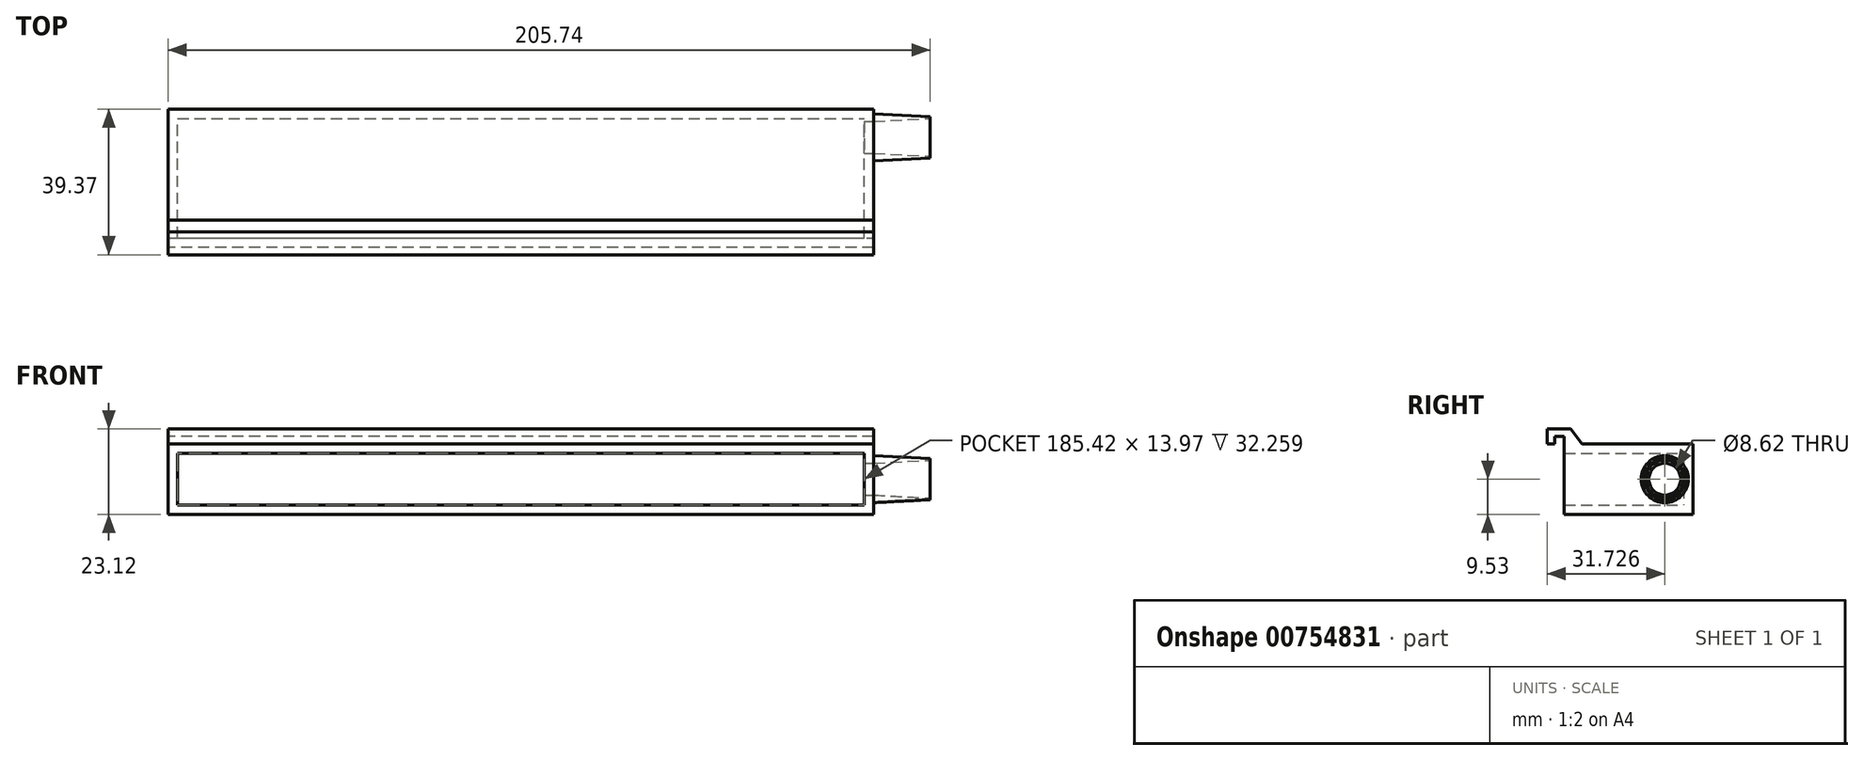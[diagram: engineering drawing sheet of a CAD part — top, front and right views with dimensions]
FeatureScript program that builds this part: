
annotation { "Feature Type Name" : "Feature", "Feature Type Description" : "" }
export const myFeature = defineFeature(function(context is Context, id is Id, definition is map)
    precondition{}
    {
        {
            var Q0;
            Q0=qCreatedBy(makeId("Front.planeOp"),FACE);
            var sketch = newSketch(context, id + "F0", { "sketchPlane" : qUnion([Q0])});
            skLineSegment(sketch, "E0.bottom", {"start": v(-95.25, 9.52) * mm, "end": v(95.25, 9.52) * mm});
            skLineSegment(sketch, "E0.top", {"start": v(-95.25, -9.52) * mm, "end": v(95.25, -9.52) * mm});
            skLineSegment(sketch, "E0.left", {"start": v(-95.25, 9.52) * mm, "end": v(-95.25, -9.52) * mm});
            skLineSegment(sketch, "E0.right", {"start": v(95.25, 9.52) * mm, "end": v(95.25, -9.52) * mm});
            skPoint(sketch, "E0.middle", {"position": v(0, 0) * mm});
            skLineSegment(sketch, "E1.bottom", {"start": v(-92.7, 6.98) * mm, "end": v(92.71, 6.99) * mm});
            skLineSegment(sketch, "E1.top", {"start": v(-92.71, -6.99) * mm, "end": v(92.7, -6.98) * mm});
            skLineSegment(sketch, "E1.left", {"start": v(-92.7, 6.98) * mm, "end": v(-92.7, -6.99) * mm});
            skLineSegment(sketch, "E1.right", {"start": v(92.71, 6.99) * mm, "end": v(92.71, -6.98) * mm});
            skSolve(sketch);
        }
        {
            var Q0;
            Q0=makeQuery(id+"F0.imprint","IMPRINT",FACE,{"disambiguationData":[TD([[makeQuery(id+"F0.imprint","IMPRINT",EDGE,{"derivedFrom":sQuery(id+"F0.wireOp",EDGE,"E0.bottom")}),-1.0]])]});
            extrude(context, id + "F1", {"entities" : qUnion([Q0]), "depth" : 63.5 * mm, "offsetDistance" : 25.4 * mm});
        }
        {
            var Q0;
            Q0=makeQuery(id+"F0.imprint","IMPRINT",FACE,{"disambiguationData":[TD([[makeQuery(id+"F0.imprint","IMPRINT",EDGE,{"derivedFrom":sQuery(id+"F0.wireOp",EDGE,"E1.bottom")}),-1.0]])]});
            extrude(context, id + "F2", {"entities" : qUnion([Q0]), "operationType" : NewBodyOperationType.ADD, "depth" : 2.54 * mm, "offsetDistance" : 25.4 * mm});
        }
        {
            var Q0;
            Q0=makeQuery(id+"F1.opExtrude","SWEPT_FACE",FACE,{"disambiguationData":[OSD([sQuery(id+"F0.wireOp",EDGE,"E0.right")])]});
            var sketch = newSketch(context, id + "F3", { "sketchPlane" : qUnion([Q0])});
            skCircle(sketch, "E2", {"center": v(-7.64, 0) * mm, "radius": 6.35 * mm});
            skCircle(sketch, "E3", {"center": v(-7.64, 0) * mm, "radius": 4.31 * mm});
            skSolve(sketch);
        }
        {
            var Q0;
            Q0=makeQuery(id+"F3.imprint","IMPRINT",FACE,{"disambiguationData":[TD([[makeQuery(id+"F3.imprint","IMPRINT",EDGE,{"derivedFrom":sQuery(id+"F3.wireOp",EDGE,"E3")}),1.0]])]});
            extrude(context, id + "F4", {"entities" : qUnion([Q0]), "operationType" : NewBodyOperationType.REMOVE, "oppositeDirection" : true, "depth" : 25.4 * mm, "offsetDistance" : 25.4 * mm});
        }
        {
            var Q0;
            Q0=makeQuery(id+"F3.imprint","IMPRINT",FACE,{"disambiguationData":[TD([[makeQuery(id+"F3.imprint","IMPRINT",EDGE,{"derivedFrom":sQuery(id+"F3.wireOp",EDGE,"E2")}),1.0]])]});
            extrude(context, id + "F5", {"entities" : qUnion([Q0]), "operationType" : NewBodyOperationType.ADD, "depth" : 15.24 * mm, "offsetDistance" : 25.4 * mm, "hasDraft" : true, "draftAngle" : 3 * degree, "draftPullDirection" : true});
        }
        {
            var Q0;
            Q0=makeQuery(id+"F1.opExtrude","SWEPT_FACE",FACE,{"disambiguationData":[OSD([sQuery(id+"F0.wireOp",EDGE,"E0.bottom")])]});
            var sketch = newSketch(context, id + "F6", { "sketchPlane" : qUnion([Q0])});
            skLineSegment(sketch, "E4", {"start": v(-95.25, -63.5) * mm, "end": v(-95.25, -68.3) * mm});
            skLineSegment(sketch, "E5", {"start": v(-95.25, -68.3) * mm, "end": v(-89.5, -68.3) * mm});
            skLineSegment(sketch, "E6", {"start": v(-89.5, -68.3) * mm, "end": v(-89.5, -66.04) * mm});
            skLineSegment(sketch, "E7", {"start": v(-89.5, -66.04) * mm, "end": v(-92.73, -66.04) * mm});
            skLineSegment(sketch, "E8", {"start": v(-92.73, -66.04) * mm, "end": v(-92.73, -63.5) * mm});
            skLineSegment(sketch, "E9", {"start": v(-92.73, -63.5) * mm, "end": v(-95.25, -63.5) * mm});
            skSolve(sketch);
        }
        {
            var Q0;
            Q0=makeQuery(id+"F6.imprint","IMPRINT",FACE,{"disambiguationData":[TD([[makeQuery(id+"F6.imprint","IMPRINT",EDGE,{"derivedFrom":sQuery(id+"F6.wireOp",EDGE,"E4")}),1.0]])]});
            extrude(context, id + "F7", {"entities" : qUnion([Q0]), "operationType" : NewBodyOperationType.ADD, "oppositeDirection" : true, "depth" : 19.05 * mm, "offsetDistance" : 25.4 * mm});
        }
        {
            var Q0;
            Q0=makeQuery(id+"F1.opExtrude","CAP_FACE",FACE,{"disambiguationData":[OSD([sQuery(id+"F0.wireOp",EDGE,"E0.bottom"),sQuery(id+"F0.wireOp",EDGE,"E0.top"),sQuery(id+"F0.wireOp",EDGE,"E0.left"),sQuery(id+"F0.wireOp",EDGE,"E0.right"),sQuery(id+"F0.wireOp",EDGE,"E1.bottom"),sQuery(id+"F0.wireOp",EDGE,"E1.top"),sQuery(id+"F0.wireOp",EDGE,"E1.left"),sQuery(id+"F0.wireOp",EDGE,"E1.right")])],"isStart":false});
            var sketch = newSketch(context, id + "F8", { "sketchPlane" : qUnion([Q0])});
            skLineSegment(sketch, "E10.bottom", {"start": v(-92.73, 9.52) * mm, "end": v(92.73, 9.52) * mm});
            skLineSegment(sketch, "E10.top", {"start": v(-92.73, 7.05) * mm, "end": v(92.73, 7.05) * mm});
            skLineSegment(sketch, "E10.left", {"start": v(-92.73, 9.52) * mm, "end": v(-92.73, 7.05) * mm});
            skLineSegment(sketch, "E10.right", {"start": v(92.73, 9.52) * mm, "end": v(92.73, 7.05) * mm});
            skPoint(sketch, "E10.middle", {"position": v(0, 8.29) * mm});
            skPoint(sketch, "E10.middle.positionSnap0", {"position": v(0, 6.99) * mm});
            skPoint(sketch, "E10.centerSnap0", {"position": v(0, 6.99) * mm});
            skSolve(sketch);
        }
        {
            var Q0;
            Q0=makeQuery(id+"F8.imprint","IMPRINT",FACE,{"disambiguationData":[TD([[makeQuery(id+"F8.imprint","IMPRINT",EDGE,{"derivedFrom":sQuery(id+"F8.wireOp",EDGE,"E10.bottom")}),-1.0]])]});
            extrude(context, id + "F9", {"entities" : qUnion([Q0]), "operationType" : NewBodyOperationType.ADD, "depth" : 12.7 * mm, "offsetDistance" : 25.4 * mm, "hasDraft" : true, "draftAngle" : 3 * degree, "draftPullDirection" : true});
        }
        {
            var Q0;
            Q0=qCreatedBy(makeId("Right.planeOp"),FACE);
            var sketch = newSketch(context, id + "F10", { "sketchPlane" : qUnion([Q0])});
            skLineSegment(sketch, "E11.bottom", {"start": v(-116.12, 21.47) * mm, "end": v(-34.8, 21.47) * mm});
            skLineSegment(sketch, "E11.top", {"start": v(-116.12, -21.47) * mm, "end": v(-34.8, -21.47) * mm});
            skLineSegment(sketch, "E11.left", {"start": v(-116.12, 21.47) * mm, "end": v(-116.12, -21.47) * mm});
            skLineSegment(sketch, "E11.right", {"start": v(-34.8, 21.47) * mm, "end": v(-34.8, -21.47) * mm});
            skPoint(sketch, "E11.middle", {"position": v(-75.46, 0) * mm});
            skSolve(sketch);
        }
        {
            var Q0;
            Q0=makeQuery(id+"F10.imprint","IMPRINT",FACE,{"disambiguationData":[TD([[makeQuery(id+"F10.imprint","IMPRINT",EDGE,{"derivedFrom":sQuery(id+"F10.wireOp",EDGE,"E11.bottom")}),-1.0]])]});
            extrude(context, id + "F11", {"entities" : qUnion([Q0]), "operationType" : NewBodyOperationType.REMOVE, "endBound" : BoundingType.SYMMETRIC, "oppositeDirection" : true, "depth" : 203.2 * mm, "offsetDistance" : 25.4 * mm});
        }
        {
            var Q0;
            Q0=makeQuery(id+"F7.boolean.opBoolean","MERGE",FACE,{"derivedFrom":[makeQuery(id+"F1.opExtrude","SWEPT_FACE",FACE,{"disambiguationData":[OSD([sQuery(id+"F0.wireOp",EDGE,"E0.left")])]}),makeQuery(id+"F7.opExtrude","SWEPT_FACE",FACE,{"disambiguationData":[OSD([sQuery(id+"F6.wireOp",EDGE,"E4")])]})]});
            var sketch = newSketch(context, id + "F12", { "sketchPlane" : qUnion([Q0])});
            skLineSegment(sketch, "E12", {"start": v(37.34, 9.53) * mm, "end": v(39.37, 9.53) * mm});
            skLineSegment(sketch, "E13", {"start": v(39.37, 9.53) * mm, "end": v(39.37, 13.59) * mm});
            skLineSegment(sketch, "E14", {"start": v(39.37, 13.59) * mm, "end": v(33.1, 13.59) * mm});
            skLineSegment(sketch, "E15", {"start": v(33.1, 13.59) * mm, "end": v(30.02, 9.53) * mm});
            skLineSegment(sketch, "E16", {"start": v(30.02, 9.53) * mm, "end": v(34.8, 9.53) * mm});
            skLineSegment(sketch, "E17", {"start": v(34.8, 9.53) * mm, "end": v(34.8, 11.56) * mm});
            skLineSegment(sketch, "E18", {"start": v(34.8, 11.56) * mm, "end": v(37.34, 11.56) * mm});
            skLineSegment(sketch, "E19", {"start": v(37.34, 11.56) * mm, "end": v(37.34, 9.53) * mm});
            skSolve(sketch);
        }
        {
            var Q0;
            Q0=makeQuery(id+"F12.imprint","IMPRINT",FACE,{"disambiguationData":[TD([[makeQuery(id+"F12.imprint","IMPRINT",EDGE,{"derivedFrom":sQuery(id+"F12.wireOp",EDGE,"E12")}),1.0]])]});
            var Q1;
            Q1=makeQuery(id+"FfIuBDjKk3I5A2u_1.1.F7.boolean.opBoolean","MERGE",FACE,{"derivedFrom":[makeQuery(id+"F1.opExtrude","SWEPT_FACE",FACE,{"disambiguationData":[OSD([sQuery(id+"F0.wireOp",EDGE,"E0.right")])]}),makeQuery(id+"FfIuBDjKk3I5A2u_1.1.F7.opExtrude","SWEPT_FACE",FACE,{"disambiguationData":[OSD([sQuery(id+"F6.wireOp",EDGE,"E4")])]})]});
            extrude(context, id + "F13", {"entities" : qUnion([Q0]), "operationType" : NewBodyOperationType.ADD, "endBound" : BoundingType.UP_TO_SURFACE, "oppositeDirection" : true, "depth" : 25.4 * mm, "endBoundEntityFace" : qUnion([Q1]), "offsetDistance" : 25.4 * mm});
        }
    });
